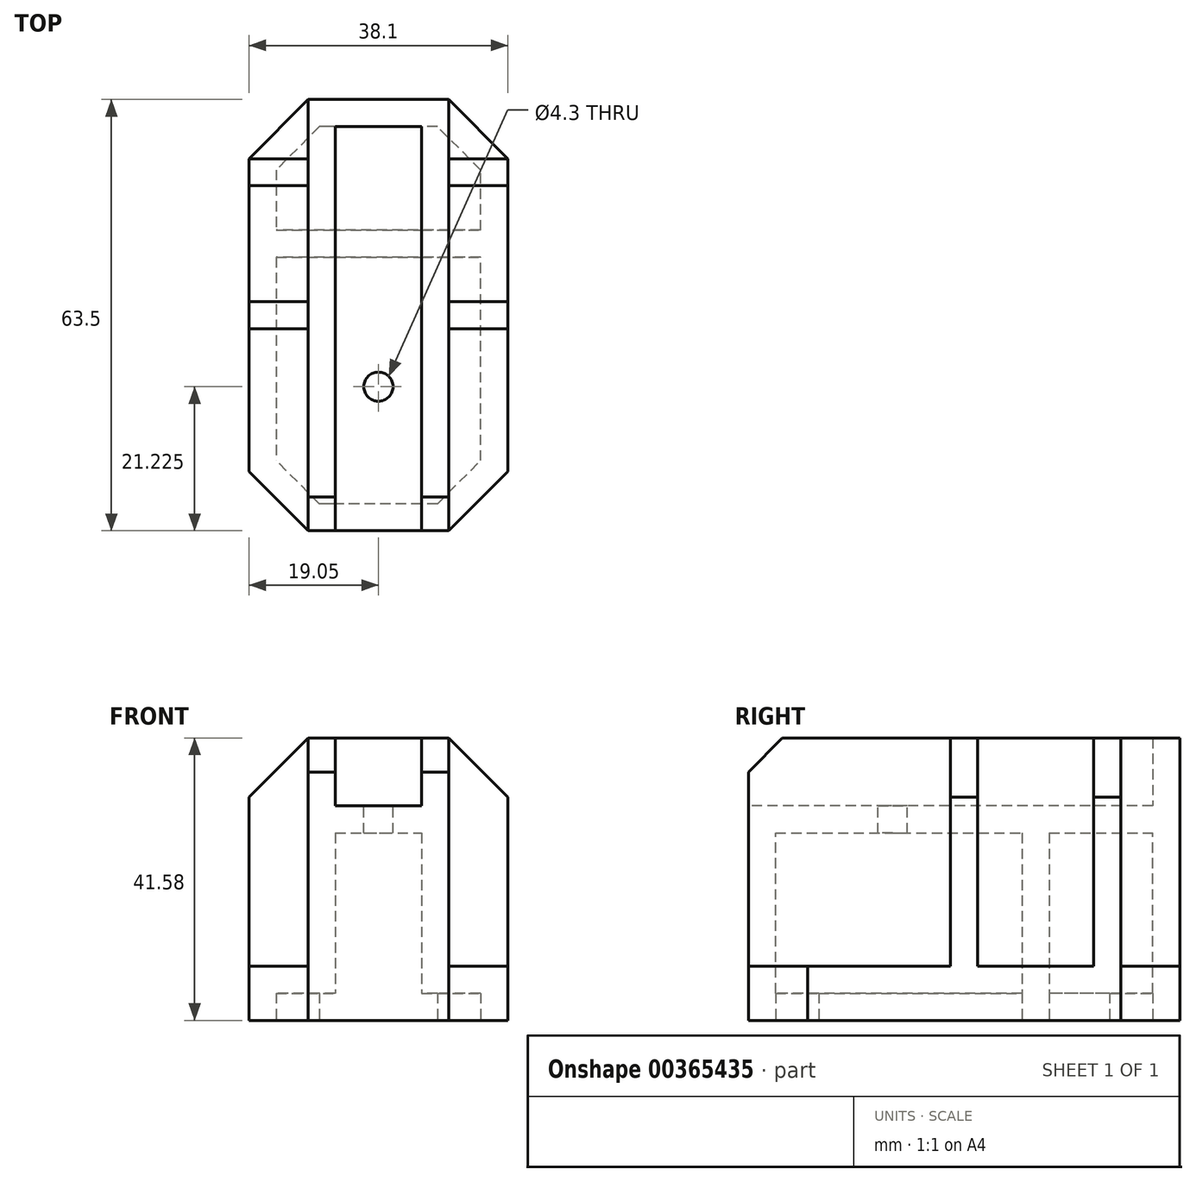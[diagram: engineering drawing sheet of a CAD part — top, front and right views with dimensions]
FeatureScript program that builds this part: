
annotation { "Feature Type Name" : "Feature", "Feature Type Description" : "" }
export const myFeature = defineFeature(function(context is Context, id is Id, definition is map)
    precondition{}
    {
        {
            var Q0;
            Q0=qCreatedBy(makeId("Front.planeOp"),FACE);
            var sketch = newSketch(context, id + "F0", { "sketchPlane" : qUnion([Q0])});
            skLineSegment(sketch, "E0.bottom", {"start": v(10.35, 0) * mm, "end": v(-10.35, 0) * mm});
            skLineSegment(sketch, "E0.top", {"start": v(10.35, 31.57) * mm, "end": v(-10.35, 31.57) * mm});
            skLineSegment(sketch, "E0.left", {"start": v(10.35, 0) * mm, "end": v(10.35, 31.57) * mm});
            skLineSegment(sketch, "E0.right", {"start": v(-10.35, 0) * mm, "end": v(-10.35, 31.57) * mm});
            skPoint(sketch, "E0.middle", {"position": v(0, 15.79) * mm});
            skLineSegment(sketch, "E1", {"start": v(-10.35, 31.57) * mm, "end": v(-10.35, 41.58) * mm});
            skLineSegment(sketch, "E2", {"start": v(-10.35, 41.58) * mm, "end": v(-6.35, 41.58) * mm});
            skLineSegment(sketch, "E3", {"start": v(-6.35, 41.58) * mm, "end": v(-6.35, 31.57) * mm});
            skLineSegment(sketch, "E4", {"start": v(0, 31.57) * mm, "end": v(0, 41.58) * mm, "construction": true});
            skLineSegment(sketch, "E5.MirrorCS", {"start": v(6.35, 41.58) * mm, "end": v(6.35, 31.57) * mm});
            skLineSegment(sketch, "E6.MirrorCS", {"start": v(10.35, 41.58) * mm, "end": v(6.35, 41.58) * mm});
            skLineSegment(sketch, "E7.MirrorCS", {"start": v(10.35, 31.57) * mm, "end": v(10.35, 41.58) * mm});
            skSolve(sketch);
        }
        {
            var Q0;
            Q0=makeQuery(id+"F0.imprint","IMPRINT",FACE,{"disambiguationData":[TD([[makeQuery(id+"F0.imprint","IMPRINT",EDGE,{"derivedFrom":sQuery(id+"F0.wireOp",EDGE,"E0.bottom")}),-1.0]])]});
            extrude(context, id + "F1", {"entities" : qUnion([Q0]), "endBound" : BoundingType.SYMMETRIC, "depth" : 63.5 * mm});
        }
        {
            var Q0;
            Q0=makeQuery(id+"F1.opExtrude","SWEPT_FACE",FACE,{"disambiguationData":[OSD([sQuery(id+"F0.wireOp",EDGE,"E0.bottom")])]});
            shell(context, id + "F2", {"entities" : qUnion([Q0]), "thickness" : 4 * mm});
        }
        {
            var Q0;
            Q0=makeQuery(id+"F1.opExtrude","CAP_FACE",FACE,{"disambiguationData":[OSD([sQuery(id+"F0.wireOp",EDGE,"E0.bottom"),sQuery(id+"F0.wireOp",EDGE,"E0.top"),sQuery(id+"F0.wireOp",EDGE,"E0.left"),sQuery(id+"F0.wireOp",EDGE,"E0.right")])],"isStart":false});
            var sketch = newSketch(context, id + "F3", { "sketchPlane" : qUnion([Q0])});
            skLineSegment(sketch, "E8.0", {"start": v(-10.35, 31.57) * mm, "end": v(-10.35, 41.58) * mm});
            skLineSegment(sketch, "E9.0", {"start": v(-10.35, 41.58) * mm, "end": v(-6.35, 41.58) * mm});
            skLineSegment(sketch, "E10.0", {"start": v(-6.35, 41.58) * mm, "end": v(-6.35, 31.57) * mm});
            skLineSegment(sketch, "E11.0", {"start": v(6.35, 41.58) * mm, "end": v(6.35, 31.57) * mm});
            skLineSegment(sketch, "E12.0", {"start": v(10.35, 41.58) * mm, "end": v(6.35, 41.58) * mm});
            skLineSegment(sketch, "E13.0", {"start": v(10.35, 31.57) * mm, "end": v(10.35, 41.58) * mm});
            skSolve(sketch);
        }
        {
            var Q0;
            {var subQ0=sQuery(id+"F3.wireOp",EDGE,"E8.0");Q0=makeQuery(id+"F3.imprint","IMPRINT",FACE,{"disambiguationData":[TD([[makeQuery(id+"F3.imprint","IMPRINT",EDGE,{"derivedFrom":subQ0}),-1.0]])]});}
            var Q1;
            {var subQ0=sQuery(id+"F3.wireOp",EDGE,"E11.0");Q1=makeQuery(id+"F3.imprint","IMPRINT",FACE,{"disambiguationData":[TD([[makeQuery(id+"F3.imprint","IMPRINT",EDGE,{"derivedFrom":subQ0}),1.0]])]});}
            var Q2;
            Q2=makeQuery(id+"F1.opExtrude","CAP_FACE",FACE,{"disambiguationData":[OSD([sQuery(id+"F0.wireOp",EDGE,"E0.bottom"),sQuery(id+"F0.wireOp",EDGE,"E0.top"),sQuery(id+"F0.wireOp",EDGE,"E0.left"),sQuery(id+"F0.wireOp",EDGE,"E0.right")])],"isStart":true});
            extrude(context, id + "F4", {"entities" : qUnion([Q0, Q1]), "operationType" : NewBodyOperationType.ADD, "endBound" : BoundingType.UP_TO_SURFACE, "oppositeDirection" : true, "endBoundEntityFace" : qUnion([Q2]), "depth" : 25 * mm});
        }
        {
            var Q0;
            Q0=qCreatedBy(makeId("Top.planeOp"),FACE);
            var sketch = newSketch(context, id + "F5", { "sketchPlane" : qUnion([Q0])});
            skLineSegment(sketch, "E14.0", {"start": v(-10.35, -31.75) * mm, "end": v(-10.35, 31.75) * mm});
            skLineSegment(sketch, "E15", {"start": v(-10.35, -31.75) * mm, "end": v(-19.05, -23.05) * mm});
            skLineSegment(sketch, "E16", {"start": v(-19.05, -23.05) * mm, "end": v(-19.05, 23.05) * mm});
            skLineSegment(sketch, "E17", {"start": v(-19.05, 23.05) * mm, "end": v(-10.35, 31.75) * mm});
            skLineSegment(sketch, "E18", {"start": v(0, 31.75) * mm, "end": v(0, -31.75) * mm, "construction": true});
            skLineSegment(sketch, "E19.MirrorCS", {"start": v(10.35, -31.75) * mm, "end": v(10.35, 31.75) * mm});
            skLineSegment(sketch, "E20.MirrorCS", {"start": v(10.35, -31.75) * mm, "end": v(19.05, -23.05) * mm});
            skLineSegment(sketch, "E21.MirrorCS", {"start": v(19.05, -23.05) * mm, "end": v(19.05, 23.05) * mm});
            skLineSegment(sketch, "E22.MirrorCS", {"start": v(19.05, 23.05) * mm, "end": v(10.35, 31.75) * mm});
            skSolve(sketch);
        }
        {
            var Q0;
            Q0=qSketchRegion(id+"F5",true);
            extrude(context, id + "F6", {"entities" : qUnion([Q0]), "operationType" : NewBodyOperationType.ADD, "depth" : 8 * mm});
        }
        {
            var Q0;
            Q0=qCreatedBy(makeId("Front.planeOp"),FACE);
            var sketch = newSketch(context, id + "F7", { "sketchPlane" : qUnion([Q0])});
            skLineSegment(sketch, "E23.0.1", {"start": v(-10.35, 8) * mm, "end": v(-10.35, 41.58) * mm});
            skLineSegment(sketch, "E23.0.3", {"start": v(-10.35, 41.58) * mm, "end": v(-10.35, 8) * mm});
            skLineSegment(sketch, "E24.0.0", {"start": v(-10.35, 8) * mm, "end": v(-19.05, 8) * mm});
            skLineSegment(sketch, "E24.0.2", {"start": v(-19.05, 8) * mm, "end": v(-10.35, 8) * mm});
            skLineSegment(sketch, "E25", {"start": v(0, 0) * mm, "end": v(0, 41.58) * mm, "construction": true});
            skLineSegment(sketch, "E26.MirrorCS", {"start": v(19.05, 8) * mm, "end": v(10.35, 8) * mm});
            skLineSegment(sketch, "E27.MirrorCS", {"start": v(10.35, 41.58) * mm, "end": v(10.35, 8) * mm});
            skLineSegment(sketch, "E28", {"start": v(19.05, 8) * mm, "end": v(19.05, 32.88) * mm});
            skLineSegment(sketch, "E29", {"start": v(19.05, 32.87) * mm, "end": v(10.35, 41.58) * mm});
            skLineSegment(sketch, "E30.MirrorCS", {"start": v(-19.05, 8) * mm, "end": v(-19.05, 32.88) * mm});
            skLineSegment(sketch, "E31.MirrorCS", {"start": v(-19.05, 32.87) * mm, "end": v(-10.35, 41.58) * mm});
            skSolve(sketch);
        }
        {
            var Q0;
            Q0=qSketchRegion(id+"F7",true);
            extrude(context, id + "F8", {"entities" : qUnion([Q0]), "operationType" : NewBodyOperationType.ADD, "endBound" : BoundingType.SYMMETRIC, "depth" : 4 * mm});
        }
        {
            var Q0;
            Q0=qCreatedBy(makeId("Front.planeOp"),FACE);
            var Q1;
            Q1=makeQuery(id+"F6.opExtrude","CAP_VERTEX",VERTEX,{"disambiguationData":[OSD([sQuery(id+"F5.wireOp",EDGE,"E21.MirrorCS"),sQuery(id+"F5.wireOp",EDGE,"E22.MirrorCS")])],"isStart":false});
            cPlane(context, id + "F9", {"entities" : qUnion([Q0, Q1]), "cplaneType" : CPlaneType.PLANE_POINT, "offset" : 25 * mm, "width" : 150 * mm, "height" : 150 * mm});
        }
        {
            var Q0;
            Q0=qCreatedBy(id+"F9.planeOp",FACE);
            var sketch = newSketch(context, id + "F10", { "sketchPlane" : qUnion([Q0])});
            skLineSegment(sketch, "E32.0", {"start": v(19.05, 8) * mm, "end": v(10.35, 8) * mm});
            skLineSegment(sketch, "E33.0", {"start": v(19.05, 8) * mm, "end": v(19.05, 32.88) * mm});
            skLineSegment(sketch, "E34.0", {"start": v(10.35, 41.58) * mm, "end": v(10.35, 8) * mm});
            skLineSegment(sketch, "E34.1", {"start": v(19.05, 32.87) * mm, "end": v(10.35, 41.58) * mm});
            skLineSegment(sketch, "E35.0", {"start": v(-19.05, 8) * mm, "end": v(-10.35, 8) * mm});
            skLineSegment(sketch, "E36.0", {"start": v(-10.35, 41.58) * mm, "end": v(-10.35, 8) * mm});
            skLineSegment(sketch, "E37.0", {"start": v(-19.05, 8) * mm, "end": v(-19.05, 32.88) * mm});
            skLineSegment(sketch, "E38.0", {"start": v(-19.05, 32.87) * mm, "end": v(-10.35, 41.58) * mm});
            skSolve(sketch);
        }
        {
            var Q0;
            Q0=qSketchRegion(id+"F10",true);
            extrude(context, id + "F11", {"entities" : qUnion([Q0]), "operationType" : NewBodyOperationType.ADD, "depth" : 4 * mm});
        }
        {
            var Q0;
            Q0=makeQuery(id+"F6.boolean.opBoolean","MERGE",FACE,{"derivedFrom":[makeQuery(id+"F1.opExtrude","SWEPT_FACE",FACE,{"disambiguationData":[OSD([sQuery(id+"F0.wireOp",EDGE,"E0.bottom")])]}),makeQuery(id+"F6.opExtrude","CAP_FACE",FACE,{"disambiguationData":[OSD([sQuery(id+"F5.wireOp",EDGE,"E14.0"),sQuery(id+"F5.wireOp",EDGE,"E15"),sQuery(id+"F5.wireOp",EDGE,"E16"),sQuery(id+"F5.wireOp",EDGE,"E17")])],"isStart":true}),makeQuery(id+"F6.opExtrude","CAP_FACE",FACE,{"disambiguationData":[OSD([sQuery(id+"F5.wireOp",EDGE,"E19.MirrorCS"),sQuery(id+"F5.wireOp",EDGE,"E20.MirrorCS"),sQuery(id+"F5.wireOp",EDGE,"E21.MirrorCS"),sQuery(id+"F5.wireOp",EDGE,"E22.MirrorCS")])],"isStart":true})]});
            var sketch = newSketch(context, id + "F12", { "sketchPlane" : qUnion([Q0])});
            skLineSegment(sketch, "E39", {"start": v(8.7, -27.75) * mm, "end": v(-8.7, -27.75) * mm});
            skLineSegment(sketch, "E40", {"start": v(-8.7, -27.75) * mm, "end": v(-15.05, -21.4) * mm});
            skLineSegment(sketch, "E41", {"start": v(-15.05, -21.4) * mm, "end": v(-15.05, 21.4) * mm});
            skLineSegment(sketch, "E42", {"start": v(8.7, 27.75) * mm, "end": v(15.05, 21.4) * mm});
            skLineSegment(sketch, "E43", {"start": v(15.05, 21.4) * mm, "end": v(15.05, -21.4) * mm});
            skLineSegment(sketch, "E44", {"start": v(15.05, -21.4) * mm, "end": v(8.7, -27.75) * mm});
            skLineSegment(sketch, "E45", {"start": v(8.7, 27.75) * mm, "end": v(-8.7, 27.75) * mm});
            skLineSegment(sketch, "E46", {"start": v(-8.7, 27.75) * mm, "end": v(-15.05, 21.4) * mm});
            skSolve(sketch);
        }
        {
            var Q0;
            Q0=qSketchRegion(id+"F12",true);
            extrude(context, id + "F13", {"entities" : qUnion([Q0]), "operationType" : NewBodyOperationType.REMOVE, "oppositeDirection" : true, "depth" : 4 * mm});
        }
        {
            var Q0;
            Q0=makeQuery(id+"F1.opExtrude","SWEPT_FACE",FACE,{"disambiguationData":[OSD([sQuery(id+"F0.wireOp",EDGE,"E0.top")])]});
            var sketch = newSketch(context, id + "F14", { "sketchPlane" : qUnion([Q0])});
            skLineSegment(sketch, "E47", {"start": v(6.35, 31.75) * mm, "end": v(6.35, 27.75) * mm});
            skLineSegment(sketch, "E48", {"start": v(6.35, 27.75) * mm, "end": v(-6.35, 27.75) * mm});
            skLineSegment(sketch, "E49", {"start": v(-6.35, 27.75) * mm, "end": v(-6.35, 31.75) * mm});
            skLineSegment(sketch, "E50", {"start": v(-6.35, 31.75) * mm, "end": v(6.35, 31.75) * mm});
            skSolve(sketch);
        }
        {
            var Q0;
            Q0=makeQuery(id+"F14.imprint","IMPRINT",FACE,{"disambiguationData":[TD([[makeQuery(id+"F14.imprint","IMPRINT",EDGE,{"derivedFrom":sQuery(id+"F14.wireOp",EDGE,"E47")}),-1.0]])]});
            var Q1;
            Q1=makeQuery(id+"F4.opExtrude","SWEPT_FACE",FACE,{"disambiguationData":[OSD([sQuery(id+"F3.wireOp",EDGE,"E9.0")])]});
            extrude(context, id + "F15", {"entities" : qUnion([Q0]), "operationType" : NewBodyOperationType.ADD, "endBound" : BoundingType.UP_TO_SURFACE, "endBoundEntityFace" : qUnion([Q1]), "depth" : 25 * mm});
        }
        {
            var Q0;
            Q0=makeQuery(id+"F4.opExtrude","CAP_EDGE",EDGE,{"disambiguationData":[OSD([sQuery(id+"F3.wireOp",EDGE,"E12.0")])],"isStart":true});
            var Q1;
            Q1=makeQuery(id+"F4.opExtrude","CAP_EDGE",EDGE,{"disambiguationData":[OSD([sQuery(id+"F3.wireOp",EDGE,"E9.0")])],"isStart":true});
            chamfer(context, id + "F16", {"entities" : qUnion([Q0, Q1]), "width" : 5 * mm, "tangentPropagation" : true});
        }
        {
            var Q0;
            Q0=makeQuery(id+"F1.opExtrude","SWEPT_FACE",FACE,{"disambiguationData":[OSD([sQuery(id+"F0.wireOp",EDGE,"E0.top")])]});
            var sketch = newSketch(context, id + "F17", { "sketchPlane" : qUnion([Q0])});
            skLineSegment(sketch, "E51", {"start": v(-6.35, -2) * mm, "end": v(6.35, -2) * mm, "construction": true});
            skLineSegment(sketch, "E52", {"start": v(-6.35, -19.05) * mm, "end": v(6.35, -19.05) * mm, "construction": true});
            skLineSegment(sketch, "E53", {"start": v(0, -2) * mm, "end": v(0, -10.53) * mm, "construction": true});
            skPoint(sketch, "E53.endSnap0", {"position": v(0, -2) * mm});
            skLineSegment(sketch, "E54", {"start": v(0, -10.53) * mm, "end": v(0, -19.05) * mm, "construction": true});
            skCircle(sketch, "E55", {"center": v(0, -10.53) * mm, "radius": 2.15 * mm});
            skSolve(sketch);
        }
        {
            var Q0;
            Q0=qSketchRegion(id+"F17",true);
            extrude(context, id + "F18", {"entities" : qUnion([Q0]), "operationType" : NewBodyOperationType.REMOVE, "oppositeDirection" : true, "depth" : 25 * mm});
        }
        {
            var Q0;
            Q0=makeQuery(id+"F6.boolean.opBoolean","MERGE",FACE,{"derivedFrom":[makeQuery(id+"F1.opExtrude","SWEPT_FACE",FACE,{"disambiguationData":[OSD([sQuery(id+"F0.wireOp",EDGE,"E0.bottom")])]}),makeQuery(id+"F6.opExtrude","CAP_FACE",FACE,{"disambiguationData":[OSD([sQuery(id+"F5.wireOp",EDGE,"E14.0"),sQuery(id+"F5.wireOp",EDGE,"E15"),sQuery(id+"F5.wireOp",EDGE,"E16"),sQuery(id+"F5.wireOp",EDGE,"E17")])],"isStart":true}),makeQuery(id+"F6.opExtrude","CAP_FACE",FACE,{"disambiguationData":[OSD([sQuery(id+"F5.wireOp",EDGE,"E19.MirrorCS"),sQuery(id+"F5.wireOp",EDGE,"E20.MirrorCS"),sQuery(id+"F5.wireOp",EDGE,"E21.MirrorCS"),sQuery(id+"F5.wireOp",EDGE,"E22.MirrorCS")])],"isStart":true})]});
            var sketch = newSketch(context, id + "F19", { "sketchPlane" : qUnion([Q0])});
            skLineSegment(sketch, "E56.bottom", {"start": v(15.05, -8.53) * mm, "end": v(-15.05, -8.53) * mm});
            skLineSegment(sketch, "E56.top", {"start": v(15.05, -12.53) * mm, "end": v(-15.05, -12.53) * mm});
            skLineSegment(sketch, "E56.left", {"start": v(15.05, -8.53) * mm, "end": v(15.05, -12.53) * mm});
            skLineSegment(sketch, "E56.right", {"start": v(-15.05, -8.53) * mm, "end": v(-15.05, -12.53) * mm});
            skPoint(sketch, "E56.middle", {"position": v(0, -10.53) * mm});
            skLineSegment(sketch, "E57", {"start": v(0, -2) * mm, "end": v(0, -19.05) * mm, "construction": true});
            skSolve(sketch);
        }
        {
            var Q0;
            Q0=qSketchRegion(id+"F19",true);
            var Q1;
            Q1=makeQuery(id+"F1.opExtrude","SWEPT_BODY",BODY,{"disambiguationData":[OSD([sQuery(id+"F0.wireOp",EDGE,"E0.bottom"),sQuery(id+"F0.wireOp",EDGE,"E0.top"),sQuery(id+"F0.wireOp",EDGE,"E0.left"),sQuery(id+"F0.wireOp",EDGE,"E0.right")])]});
            extrude(context, id + "F20", {"entities" : qUnion([Q0]), "operationType" : NewBodyOperationType.ADD, "endBound" : BoundingType.UP_TO_BODY, "oppositeDirection" : true, "endBoundEntityBody" : qUnion([Q1]), "depth" : 25 * mm});
        }
    });
